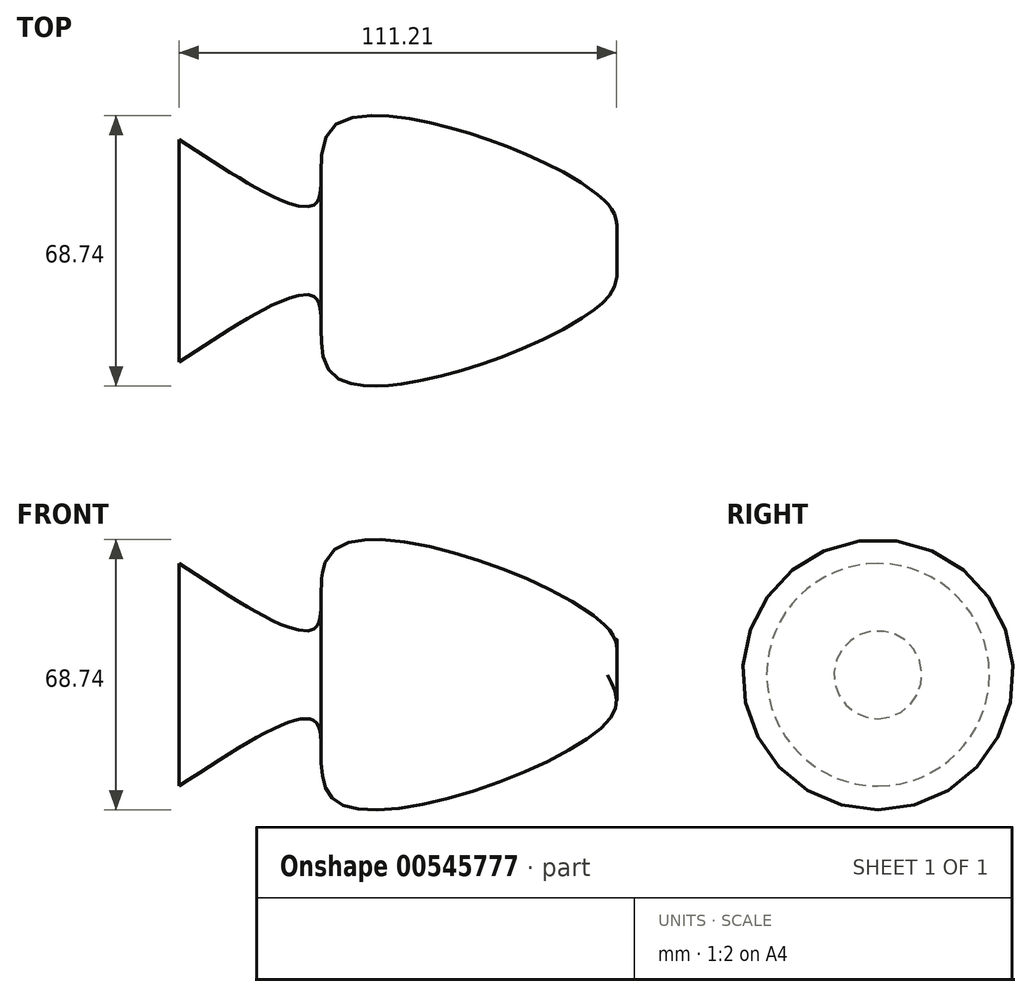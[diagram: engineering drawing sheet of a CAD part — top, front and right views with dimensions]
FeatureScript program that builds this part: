
annotation { "Feature Type Name" : "Feature", "Feature Type Description" : "" }
export const myFeature = defineFeature(function(context is Context, id is Id, definition is map)
    precondition{}
    {
        {
            var Q0;
            Q0=qCreatedBy(makeId("Front.planeOp"),FACE);
            var sketch = newSketch(context, id + "F0", { "sketchPlane" : qUnion([Q0])});
            skFitSpline(sketch, "E0", {"points": [v(73.7, 0) * mm, v(73.7, -12) * mm, v(4.71, -32.13) * mm, v(0, -12.43) * mm, v(-35.13, -28.28) * mm], "startDerivative": vector(40.59, -72.13) * mm, "endDerivative": vector(-173.16, -113.85) * mm});
            skLineSegment(sketch, "E1", {"start": v(-35.13, -28.28) * mm, "end": v(-35.13, 0) * mm});
            skLineSegment(sketch, "E2", {"start": v(-35.13, 0) * mm, "end": v(73.7, 0) * mm});
            skSolve(sketch);
        }
        {
            var Q0;
            Q0=qCreatedBy(makeId("Front.planeOp"),FACE);
            var sketch = newSketch(context, id + "F1", { "sketchPlane" : qUnion([Q0])});
            skCircle(sketch, "E3", {"center": v(8.4, -17.24) * mm, "radius": 4.95 * mm});
            skSolve(sketch);
        }
        {
            var Q0;
            Q0=qCreatedBy(makeId("Top.planeOp"),FACE);
            var sketch = newSketch(context, id + "F2", { "sketchPlane" : qUnion([Q0])});
            skFitSpline(sketch, "E4", {"points": [v(8.08, 0) * mm, v(4.09, 20.94) * mm, v(37.73, 30.83) * mm, v(56.65, 0) * mm], "startDerivative": vector(-42.29, 79.69) * mm, "endDerivative": vector(32.47, -111.7) * mm});
            skSolve(sketch);
        }
        {
            var Q0;
            Q0=makeQuery(id+"F0.imprint","IMPRINT",FACE,{"disambiguationData":[TD([[makeQuery(id+"F0.imprint","IMPRINT",EDGE,{"derivedFrom":sQuery(id+"F0.wireOp",EDGE,"E0")}),-1.0]])]});
            var Q1;
            Q1=sQuery(id+"F0.wireOp",EDGE,"E2");
            revolve(context, id + "F3", {"entities" : qUnion([Q0]), "axis" : qUnion([Q1]), "revolveType" : RevolveType.FULL});
        }
    });
